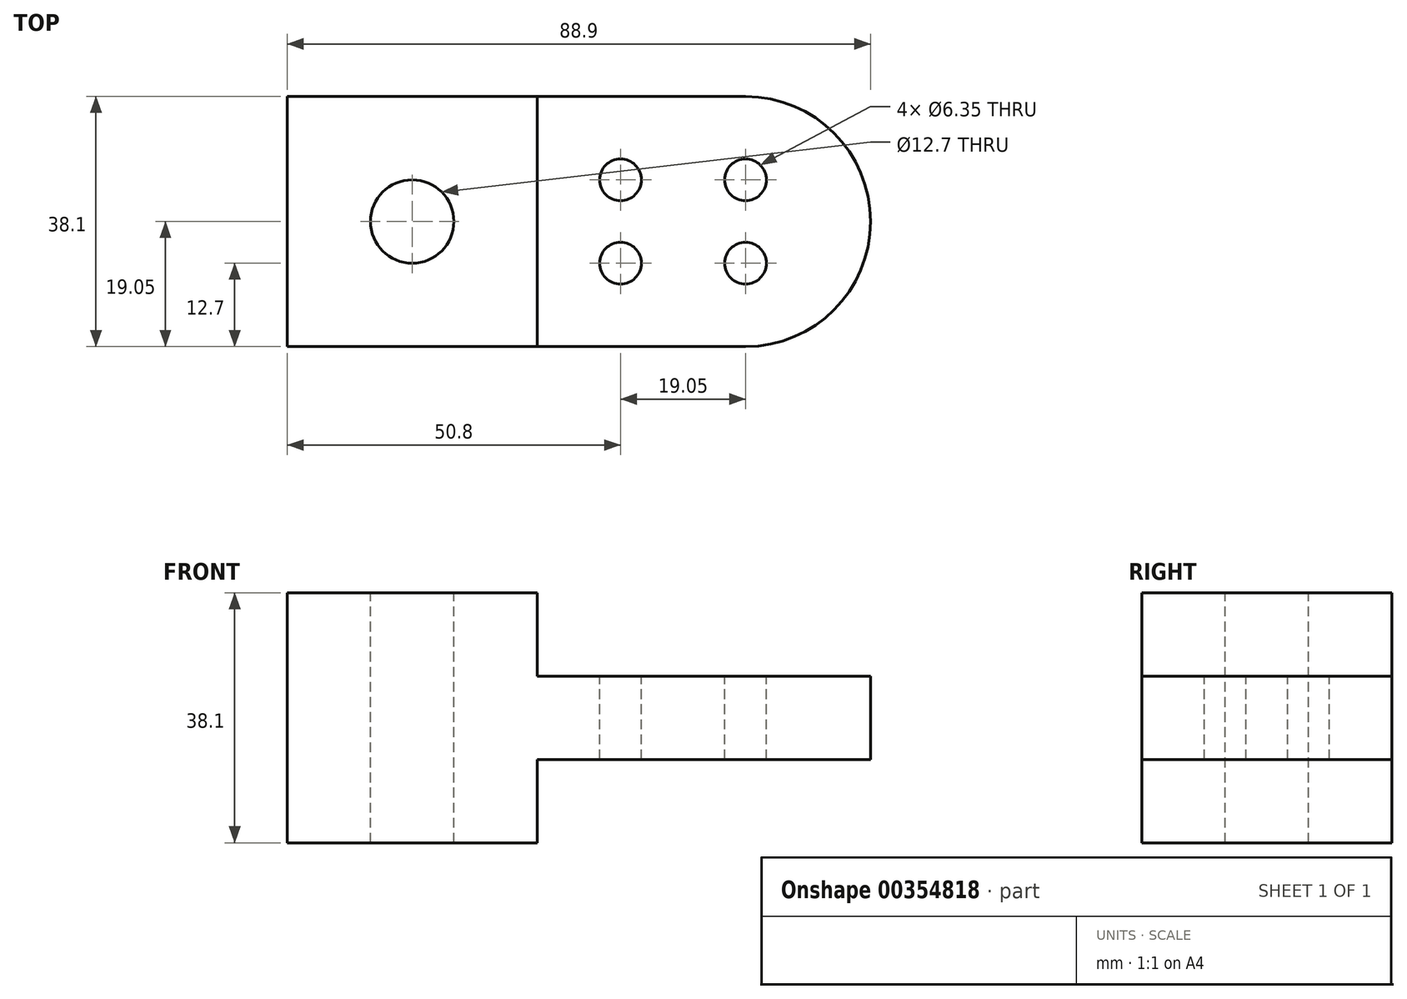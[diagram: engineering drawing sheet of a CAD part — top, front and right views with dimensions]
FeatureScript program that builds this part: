
annotation { "Feature Type Name" : "Feature", "Feature Type Description" : "" }
export const myFeature = defineFeature(function(context is Context, id is Id, definition is map)
    precondition{}
    {
        {
            var Q0;
            Q0=qCreatedBy(makeId("Front.planeOp"),FACE);
            var sketch = newSketch(context, id + "F0", { "sketchPlane" : qUnion([Q0])});
            skLineSegment(sketch, "E0", {"start": v(0, -19.05) * mm, "end": v(0, 19.05) * mm});
            skLineSegment(sketch, "E1", {"start": v(0, 19.05) * mm, "end": v(38.1, 19.05) * mm});
            skLineSegment(sketch, "E2", {"start": v(38.1, 19.05) * mm, "end": v(38.1, -19.05) * mm});
            skLineSegment(sketch, "E3", {"start": v(38.1, -19.05) * mm, "end": v(0, -19.05) * mm});
            skLineSegment(sketch, "E4", {"start": v(0, 0) * mm, "end": v(88.9, 0) * mm, "construction": true});
            skLineSegment(sketch, "E5", {"start": v(88.9, 6.35) * mm, "end": v(88.9, -6.35) * mm});
            skLineSegment(sketch, "E6", {"start": v(88.9, 6.35) * mm, "end": v(38.1, 6.35) * mm});
            skLineSegment(sketch, "E7", {"start": v(88.9, -6.35) * mm, "end": v(38.1, -6.35) * mm});
            skSolve(sketch);
        }
        {
            var Q0;
            Q0 = qSketchRegion(id + "F0", true);
            extrude(context, id + "F1", {"entities" : qUnion([Q0]), "endBound" : BoundingType.SYMMETRIC, "depth" : 38.1 * mm});
        }
        {
            var Q0;
            Q0=makeQuery(id+"F1.opExtrude","SWEPT_FACE",FACE,{"disambiguationData":[OSD([sQuery(id+"F0.wireOp",EDGE,"E1")])]});
            var sketch = newSketch(context, id + "F2", { "sketchPlane" : qUnion([Q0])});
            skLineSegment(sketch, "E8", {"start": v(0, 0) * mm, "end": v(38.1, 0) * mm, "construction": true});
            skPoint(sketch, "E9", {"position": v(19.05, 0) * mm});
            skCircle(sketch, "E10", {"center": v(19.05, 0) * mm, "radius": 6.35 * mm});
            skSolve(sketch);
        }
        {
            var Q0;
            Q0 = qSketchRegion(id + "F2", true);
            extrude(context, id + "F3", {"entities" : qUnion([Q0]), "operationType" : NewBodyOperationType.REMOVE, "endBound" : BoundingType.THROUGH_ALL, "oppositeDirection" : true, "depth" : 25.4 * mm});
        }
        {
            var Q0;
            Q0=makeQuery(id+"F1.opExtrude","SWEPT_FACE",FACE,{"disambiguationData":[OSD([sQuery(id+"F0.wireOp",EDGE,"E6")])]});
            var sketch = newSketch(context, id + "F4", { "sketchPlane" : qUnion([Q0])});
            skLineSegment(sketch, "E11", {"start": v(38.1, 19.05) * mm, "end": v(69.85, 19.05) * mm});
            skLineSegment(sketch, "E12", {"start": v(38.1, -19.05) * mm, "end": v(69.85, -19.05) * mm});
            skArc(sketch, "E13", {"start": v(69.85, -19.05) * mm, "mid": v(88.9, 0) * mm, "end": v(69.85, 19.05) * mm});
            skLineSegment(sketch, "E14", {"start": v(69.85, 19.05) * mm, "end": v(88.9, 19.05) * mm});
            skLineSegment(sketch, "E15", {"start": v(88.9, 19.05) * mm, "end": v(88.9, 0) * mm});
            skLineSegment(sketch, "E16", {"start": v(88.9, 0) * mm, "end": v(88.9, -19.05) * mm});
            skLineSegment(sketch, "E17", {"start": v(88.9, -19.05) * mm, "end": v(69.85, -19.05) * mm});
            skPoint(sketch, "E18", {"position": v(50.8, 6.35) * mm});
            skPoint(sketch, "E19", {"position": v(69.85, 6.35) * mm});
            skPoint(sketch, "E20", {"position": v(50.8, -6.35) * mm});
            skPoint(sketch, "E21", {"position": v(69.85, -6.35) * mm});
            skCircle(sketch, "E22", {"center": v(50.8, 6.35) * mm, "radius": 3.18 * mm});
            skCircle(sketch, "E23", {"center": v(69.85, 6.35) * mm, "radius": 3.18 * mm});
            skCircle(sketch, "E24", {"center": v(69.85, -6.35) * mm, "radius": 3.18 * mm});
            skCircle(sketch, "E25", {"center": v(50.8, -6.35) * mm, "radius": 3.18 * mm});
            skSolve(sketch);
        }
        {
            var Q0;
            Q0 = qSketchRegion(id + "F4", true);
            extrude(context, id + "F5", {"entities" : qUnion([Q0]), "operationType" : NewBodyOperationType.REMOVE, "endBound" : BoundingType.THROUGH_ALL, "oppositeDirection" : true, "depth" : 25.4 * mm});
        }
    });
